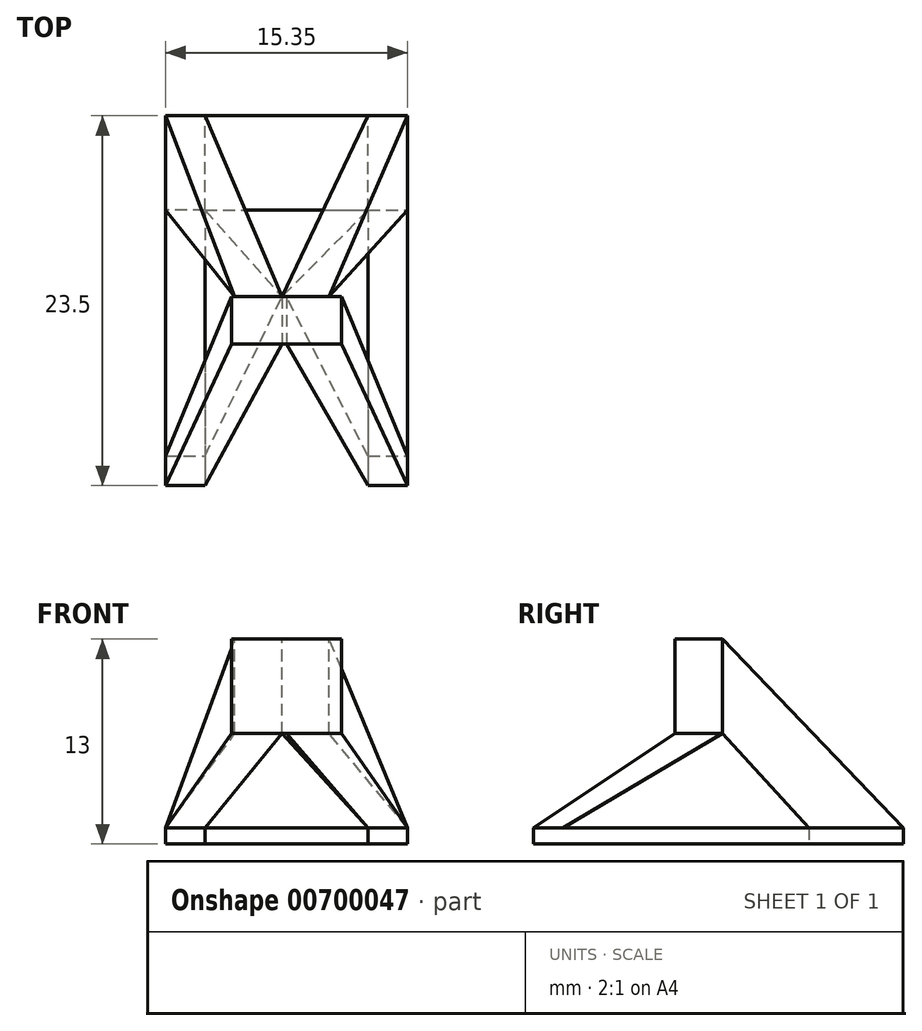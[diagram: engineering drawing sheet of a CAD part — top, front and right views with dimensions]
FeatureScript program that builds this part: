
annotation { "Feature Type Name" : "Feature", "Feature Type Description" : "" }
export const myFeature = defineFeature(function(context is Context, id is Id, definition is map)
    precondition{}
    {
        {
            var Q0;
            Q0=qCreatedBy(makeId("Top.planeOp"),FACE);
            var sketch = newSketch(context, id + "F0", { "sketchPlane" : qUnion([Q0])});
            skLineSegment(sketch, "E0.bottom", {"start": v(-7.39, 11.5) * mm, "end": v(7.96, 11.5) * mm});
            skLineSegment(sketch, "E0.top", {"start": v(-7.39, 5.5) * mm, "end": v(7.96, 5.5) * mm});
            skLineSegment(sketch, "E0.left", {"start": v(-7.39, 11.5) * mm, "end": v(-7.39, 5.5) * mm});
            skLineSegment(sketch, "E0.right", {"start": v(7.96, 11.5) * mm, "end": v(7.96, 5.5) * mm});
            skLineSegment(sketch, "E1.bottom", {"start": v(-7.39, 5.5) * mm, "end": v(-4.89, 5.5) * mm});
            skLineSegment(sketch, "E1.top", {"start": v(-7.39, -12) * mm, "end": v(-4.89, -12) * mm});
            skLineSegment(sketch, "E1.left", {"start": v(-7.39, 5.5) * mm, "end": v(-7.39, -12) * mm});
            skLineSegment(sketch, "E1.right", {"start": v(-4.89, 5.5) * mm, "end": v(-4.89, -12) * mm});
            skLineSegment(sketch, "E2.bottom", {"start": v(7.96, 5.5) * mm, "end": v(5.46, 5.5) * mm});
            skLineSegment(sketch, "E2.top", {"start": v(7.96, -12) * mm, "end": v(5.46, -12) * mm});
            skLineSegment(sketch, "E2.left", {"start": v(7.96, 5.5) * mm, "end": v(7.96, -12) * mm});
            skLineSegment(sketch, "E2.right", {"start": v(5.46, 5.5) * mm, "end": v(5.46, -12) * mm});
            skSolve(sketch);
        }
        {
            var Q0;
            Q0 = qSketchRegion(id + "F0", true);
            extrude(context, id + "F1", {"entities" : qUnion([Q0]), "depth" : 1 * mm, "offsetDistance" : 25 * mm});
        }
        {
            var Q0;
            Q0=qCreatedBy(makeId("Front.planeOp"),FACE);
            var sketch = newSketch(context, id + "F2", { "sketchPlane" : qUnion([Q0])});
            skLineSegment(sketch, "E3.bottom", {"start": v(-3.22, 13) * mm, "end": v(3.78, 13) * mm});
            skLineSegment(sketch, "E3.top", {"start": v(-3.22, 7) * mm, "end": v(3.78, 7) * mm});
            skLineSegment(sketch, "E3.left", {"start": v(-3.22, 13) * mm, "end": v(-3.22, 7) * mm});
            skLineSegment(sketch, "E3.right", {"start": v(3.78, 13) * mm, "end": v(3.78, 7) * mm});
            skSolve(sketch);
        }
        {
            var Q0;
            Q0 = qSketchRegion(id + "F2", true);
            extrude(context, id + "F3", {"entities" : qUnion([Q0]), "depth" : 3 * mm, "offsetDistance" : 25 * mm});
        }
        {
            var Q0;
            Q0=makeQuery(id+"F1.opExtrude","CAP_FACE",FACE,{"disambiguationData":[OSD([sQuery(id+"F0.wireOp",EDGE,"E0.bottom"),sQuery(id+"F0.wireOp",EDGE,"E0.top"),sQuery(id+"F0.wireOp",EDGE,"E0.left"),sQuery(id+"F0.wireOp",EDGE,"E0.right"),sQuery(id+"F0.wireOp",EDGE,"E1.top"),sQuery(id+"F0.wireOp",EDGE,"E1.left"),sQuery(id+"F0.wireOp",EDGE,"E1.right"),sQuery(id+"F0.wireOp",EDGE,"E2.top"),sQuery(id+"F0.wireOp",EDGE,"E2.left"),sQuery(id+"F0.wireOp",EDGE,"E2.right")])],"isStart":false});
            var sketch = newSketch(context, id + "F4", { "sketchPlane" : qUnion([Q0])});
            skLineSegment(sketch, "E4.bottom", {"start": v(-4.89, 5.5) * mm, "end": v(-7.39, 5.5) * mm});
            skLineSegment(sketch, "E4.top", {"start": v(-4.89, 11.5) * mm, "end": v(-7.39, 11.5) * mm});
            skLineSegment(sketch, "E4.left", {"start": v(-4.89, 5.5) * mm, "end": v(-4.89, 11.5) * mm});
            skLineSegment(sketch, "E4.right", {"start": v(-7.39, 5.5) * mm, "end": v(-7.39, 11.5) * mm});
            skLineSegment(sketch, "E5.bottom", {"start": v(5.46, 5.5) * mm, "end": v(7.96, 5.5) * mm});
            skLineSegment(sketch, "E5.top", {"start": v(5.46, 11.5) * mm, "end": v(7.96, 11.5) * mm});
            skLineSegment(sketch, "E5.left", {"start": v(5.46, 5.5) * mm, "end": v(5.46, 11.5) * mm});
            skLineSegment(sketch, "E5.right", {"start": v(7.96, 5.5) * mm, "end": v(7.96, 11.5) * mm});
            skLineSegment(sketch, "E6.bottom", {"start": v(-7.39, -12) * mm, "end": v(-4.89, -12) * mm});
            skLineSegment(sketch, "E6.top", {"start": v(-7.39, -10.1) * mm, "end": v(-4.89, -10.1) * mm});
            skLineSegment(sketch, "E6.left", {"start": v(-7.39, -12) * mm, "end": v(-7.39, -10.1) * mm});
            skLineSegment(sketch, "E6.right", {"start": v(-4.89, -12) * mm, "end": v(-4.89, -10.1) * mm});
            skLineSegment(sketch, "E7.bottom", {"start": v(5.46, -12) * mm, "end": v(7.96, -12) * mm});
            skLineSegment(sketch, "E7.top", {"start": v(5.46, -10.11) * mm, "end": v(7.96, -10.11) * mm});
            skLineSegment(sketch, "E7.left", {"start": v(5.46, -12) * mm, "end": v(5.46, -10.11) * mm});
            skLineSegment(sketch, "E7.right", {"start": v(7.96, -12) * mm, "end": v(7.96, -10.11) * mm});
            skSolve(sketch);
        }
        {
            var Q0;
            Q0=qCreatedBy(makeId("Front.planeOp"),FACE);
            var sketch = newSketch(context, id + "F5", { "sketchPlane" : qUnion([Q0])});
            skLineSegment(sketch, "E8.bottom", {"start": v(-3, 7) * mm, "end": v(0, 7) * mm});
            skLineSegment(sketch, "E8.top", {"start": v(-3, 13) * mm, "end": v(0, 13) * mm});
            skLineSegment(sketch, "E8.left", {"start": v(-3, 7) * mm, "end": v(-3, 13) * mm});
            skLineSegment(sketch, "E8.right", {"start": v(0, 7) * mm, "end": v(0, 13) * mm});
            skLineSegment(sketch, "E9.bottom", {"start": v(3, 7) * mm, "end": v(0, 7) * mm});
            skLineSegment(sketch, "E9.top", {"start": v(3, 13) * mm, "end": v(0, 13) * mm});
            skLineSegment(sketch, "E9.left", {"start": v(3, 7) * mm, "end": v(3, 13) * mm});
            skSolve(sketch);
        }
        {
            var Q0;
            Q0=makeQuery(id+"F4.imprint","IMPRINT",FACE,{"disambiguationData":[TD([[makeQuery(id+"F4.imprint","IMPRINT",EDGE,{"derivedFrom":sQuery(id+"F4.wireOp",EDGE,"E5.bottom")}),1.0]])]});
            var Q1;
            Q1=makeQuery(id+"F5.imprint","IMPRINT",FACE,{"disambiguationData":[TD([[makeQuery(id+"F5.imprint","IMPRINT",EDGE,{"derivedFrom":sQuery(id+"F5.wireOp",EDGE,"E9.bottom")}),-1.0]])]});
            loft(context, id + "F6", {"sheetProfilesArray" : [{ "sheetProfileEntities" : qUnion([Q0]) }, { "sheetProfileEntities" : qUnion([Q1]) }]});
        }
        {
            var Q0;
            Q0=makeQuery(id+"F4.imprint","IMPRINT",FACE,{"disambiguationData":[TD([[makeQuery(id+"F4.imprint","IMPRINT",EDGE,{"derivedFrom":sQuery(id+"F4.wireOp",EDGE,"E4.bottom")}),-1.0]])]});
            var Q1;
            Q1=makeQuery(id+"F5.imprint","IMPRINT",FACE,{"disambiguationData":[TD([[makeQuery(id+"F5.imprint","IMPRINT",EDGE,{"derivedFrom":sQuery(id+"F5.wireOp",EDGE,"E8.bottom")}),1.0]])]});
            loft(context, id + "F7", {"sheetProfilesArray" : [{ "sheetProfileEntities" : qUnion([Q0]) }, { "sheetProfileEntities" : qUnion([Q1]) }]});
        }
        {
            var Q0;
            Q0=makeQuery(id+"F3.opExtrude","SWEPT_FACE",FACE,{"disambiguationData":[OSD([sQuery(id+"F2.wireOp",EDGE,"E3.top")])]});
            var sketch = newSketch(context, id + "F8", { "sketchPlane" : qUnion([Q0])});
            skPoint(sketch, "E10.oppositeSnap0", {"position": v(0.28, 3) * mm});
            skLineSegment(sketch, "E10.bottom", {"start": v(-3.22, 0) * mm, "end": v(0, 0) * mm});
            skLineSegment(sketch, "E10.top", {"start": v(-3.22, 3) * mm, "end": v(0, 3) * mm});
            skLineSegment(sketch, "E10.left", {"start": v(-3.22, 0) * mm, "end": v(-3.22, 3) * mm});
            skLineSegment(sketch, "E10.right", {"start": v(0, 0) * mm, "end": v(0, 3) * mm});
            skLineSegment(sketch, "E11.bottom", {"start": v(3.78, 0) * mm, "end": v(0.28, 0) * mm});
            skLineSegment(sketch, "E11.top", {"start": v(3.78, 3) * mm, "end": v(0.28, 3) * mm});
            skLineSegment(sketch, "E11.left", {"start": v(3.78, 0) * mm, "end": v(3.78, 3) * mm});
            skLineSegment(sketch, "E11.right", {"start": v(0.28, 0) * mm, "end": v(0.28, 3) * mm});
            skSolve(sketch);
        }
        {
            var Q0;
            Q0=makeQuery(id+"F4.imprint","IMPRINT",FACE,{"disambiguationData":[TD([[makeQuery(id+"F4.imprint","IMPRINT",EDGE,{"derivedFrom":sQuery(id+"F4.wireOp",EDGE,"E6.bottom")}),1.0]])]});
            var Q1;
            Q1=makeQuery(id+"F8.imprint","IMPRINT",FACE,{"disambiguationData":[TD([[makeQuery(id+"F8.imprint","IMPRINT",EDGE,{"derivedFrom":sQuery(id+"F8.wireOp",EDGE,"E10.bottom")}),1.0]])]});
            loft(context, id + "F9", {"sheetProfilesArray" : [{ "sheetProfileEntities" : qUnion([Q0]) }, { "sheetProfileEntities" : qUnion([Q1]) }]});
        }
        {
            var Q0;
            Q0=makeQuery(id+"F4.imprint","IMPRINT",FACE,{"disambiguationData":[TD([[makeQuery(id+"F4.imprint","IMPRINT",EDGE,{"derivedFrom":sQuery(id+"F4.wireOp",EDGE,"E7.bottom")}),-1.0]])]});
            var Q1;
            Q1=makeQuery(id+"F8.imprint","IMPRINT",FACE,{"disambiguationData":[TD([[makeQuery(id+"F8.imprint","IMPRINT",EDGE,{"derivedFrom":sQuery(id+"F8.wireOp",EDGE,"E11.bottom")}),1.0]])]});
            loft(context, id + "F10", {"sheetProfilesArray" : [{ "sheetProfileEntities" : qUnion([Q0]) }, { "sheetProfileEntities" : qUnion([Q1]) }]});
        }
    });
